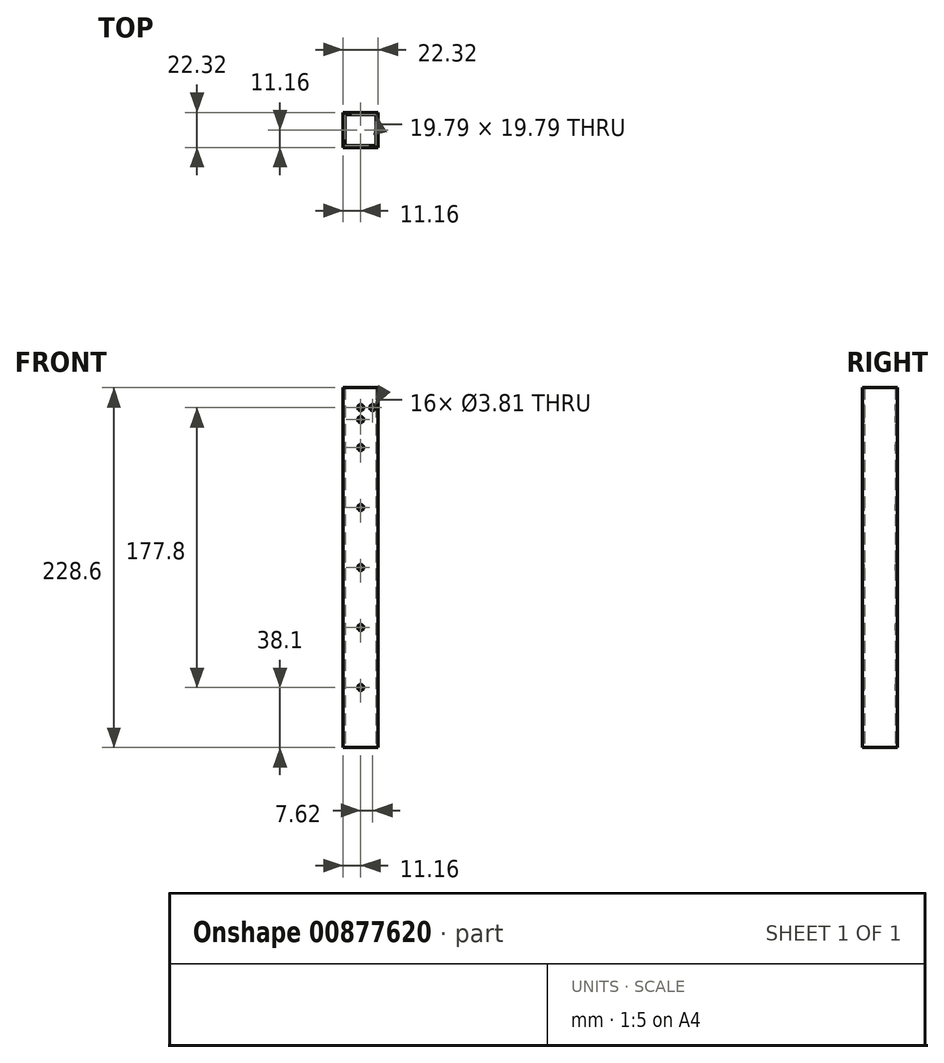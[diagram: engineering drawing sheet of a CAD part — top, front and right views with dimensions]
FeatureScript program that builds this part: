
annotation { "Feature Type Name" : "Feature", "Feature Type Description" : "" }
export const myFeature = defineFeature(function(context is Context, id is Id, definition is map)
    precondition{}
    {
        {
            var Q0;
            Q0=qCreatedBy(makeId("Top.planeOp"),FACE);
            var sketch = newSketch(context, id + "F0", { "sketchPlane" : qUnion([Q0])});
            skLineSegment(sketch, "E0.bottom", {"start": v(11.16, 11.16) * mm, "end": v(-11.16, 11.16) * mm});
            skLineSegment(sketch, "E0.top", {"start": v(11.16, -11.16) * mm, "end": v(-11.16, -11.16) * mm});
            skLineSegment(sketch, "E0.left", {"start": v(11.16, 11.16) * mm, "end": v(11.16, -11.16) * mm});
            skLineSegment(sketch, "E0.right", {"start": v(-11.16, 11.16) * mm, "end": v(-11.16, -11.16) * mm});
            skPoint(sketch, "E0.middle", {"position": v(0, 0) * mm});
            skLineSegment(sketch, "E1.bottom", {"start": v(9.9, 9.9) * mm, "end": v(-9.9, 9.9) * mm});
            skLineSegment(sketch, "E1.top", {"start": v(9.9, -9.9) * mm, "end": v(-9.9, -9.9) * mm});
            skLineSegment(sketch, "E1.left", {"start": v(9.9, 9.9) * mm, "end": v(9.9, -9.9) * mm});
            skLineSegment(sketch, "E1.right", {"start": v(-9.9, 9.9) * mm, "end": v(-9.9, -9.9) * mm});
            skSolve(sketch);
        }
        {
            var Q0;
            Q0 = qSketchRegion(id + "F0", true);
            extrude(context, id + "F1", {"entities" : qUnion([Q0]), "depth" : 228.6 * mm, "offsetDistance" : 25.4 * mm});
        }
        {
            var Q0;
            Q0=makeQuery(id+"F1.opExtrude","SWEPT_FACE",FACE,{"disambiguationData":[OSD([sQuery(id+"F0.wireOp",EDGE,"E0.top")])]});
            var sketch = newSketch(context, id + "F2", { "sketchPlane" : qUnion([Q0])});
            skCircle(sketch, "E2", {"center": v(0, 38.1) * mm, "radius": 1.9 * mm});
            skCircle(sketch, "E3.0.1.0", {"center": v(0, 76.2) * mm, "radius": 1.9 * mm});
            skCircle(sketch, "E3.0.2.0", {"center": v(0, 114.3) * mm, "radius": 1.9 * mm});
            skCircle(sketch, "E3.0.3.0", {"center": v(0, 152.4) * mm, "radius": 1.9 * mm});
            skCircle(sketch, "E3.0.4.0", {"center": v(0, 190.5) * mm, "radius": 1.9 * mm});
            skLineSegment(sketch, "E3.direction1", {"start": v(0, 38.1) * mm, "end": v(25.4, 38.1) * mm, "construction": true});
            skLineSegment(sketch, "E3.direction2", {"start": v(0, 38.1) * mm, "end": v(0, 76.2) * mm, "construction": true});
            skSolve(sketch);
        }
        {
            var Q0;
            Q0 = qSketchRegion(id + "F2", true);
            extrude(context, id + "F3", {"entities" : qUnion([Q0]), "operationType" : NewBodyOperationType.REMOVE, "endBound" : BoundingType.THROUGH_ALL, "oppositeDirection" : true, "depth" : 25.4 * mm, "offsetDistance" : 25.4 * mm});
        }
        {
            var Q0;
            Q0=makeQuery(id+"F1.opExtrude","SWEPT_FACE",FACE,{"disambiguationData":[OSD([sQuery(id+"F0.wireOp",EDGE,"E0.top")])]});
            var sketch = newSketch(context, id + "F4", { "sketchPlane" : qUnion([Q0])});
            skCircle(sketch, "E4", {"center": v(0, 215.9) * mm, "radius": 1.9 * mm});
            skCircle(sketch, "E5", {"center": v(7.62, 215.9) * mm, "radius": 1.9 * mm});
            skCircle(sketch, "E6", {"center": v(0, 208.28) * mm, "radius": 1.9 * mm});
            skSolve(sketch);
        }
        {
            var Q0;
            Q0 = qSketchRegion(id + "F4", true);
            extrude(context, id + "F5", {"entities" : qUnion([Q0]), "operationType" : NewBodyOperationType.REMOVE, "endBound" : BoundingType.THROUGH_ALL, "oppositeDirection" : true, "depth" : 25.4 * mm, "offsetDistance" : 25.4 * mm});
        }
    });
